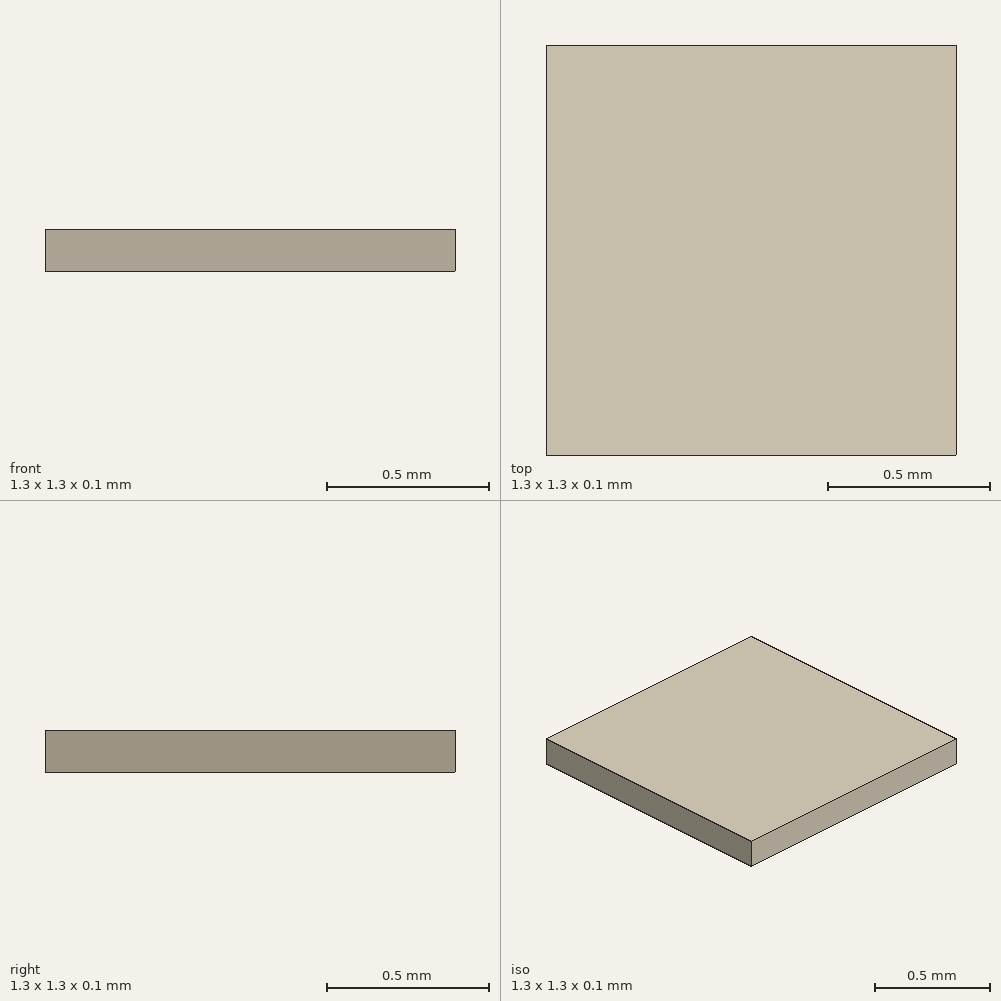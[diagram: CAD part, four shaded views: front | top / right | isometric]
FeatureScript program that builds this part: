
annotation { "Feature Type Name" : "Feature", "Feature Type Description" : "" }
export const myFeature = defineFeature(function(context is Context, id is Id, definition is map)
    precondition{}
    {
        {
            var Q0;
            Q0=qCreatedBy(makeId("Top.planeOp"),FACE);
            var sketch = newSketch(context, id + "F0", { "sketchPlane" : qUnion([Q0])});
            skLineSegment(sketch, "E0", {"start": v(0, 0) * mm, "end": v(0, 1.27) * mm});
            skLineSegment(sketch, "E1", {"start": v(0, 1.27) * mm, "end": v(1.27, 1.27) * mm});
            skLineSegment(sketch, "E2", {"start": v(1.27, 1.27) * mm, "end": v(1.27, 0) * mm});
            skLineSegment(sketch, "E3", {"start": v(1.27, 0) * mm, "end": v(0, 0) * mm});
            skSolve(sketch);
        }
        {
            var Q0;
            Q0=makeQuery(id+"F0.imprint","IMPRINT",FACE,{"disambiguationData":[TD([[makeQuery(id+"F0.imprint","IMPRINT",EDGE,{"derivedFrom":sQuery(id+"F0.wireOp",EDGE,"E0")}),-1.0]])]});
            extrude(context, id + "F1", {"entities" : qUnion([Q0]), "depth" : 0.13 * mm});
        }
    });
